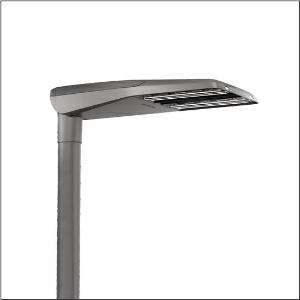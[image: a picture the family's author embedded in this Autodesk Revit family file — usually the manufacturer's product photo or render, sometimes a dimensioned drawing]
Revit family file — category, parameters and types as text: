
# Revit family: streetlight_sl_11_iq_midi___st1_0a_5xc3m41f08le_9450
name_source: partatom
category: Lighting Fixtures
units: mm (PartAtom-declared; Revit-internal decimal feet)

## family parameters
Cut with Voids When Loaded = No
Host = Face
Light Source = No
Part Type = Normal
Room Calculation Point = No
Round Connector Dimension = Use Diameter
Shared = No

## types (1)
- --- (1 x LED, 9290 lm, 60.4 W, 4000K)
    Apparent Load = 60 VA
    CIE Flux Codes = 33 66 96 100 100
    Color Rendering = 70
    Color Temperature = 4000K
    Default Elevation = 1800 mm
    Description = Streetlight SL 11 iQ midi, mast luminaire, primary light control with 3 zone facetted reflector, of plastic, silver coated, highly specular, primary optical cover: cover, of PMMA, transparent, light distribution: ST1.0a, light emission: direct distribution, primary light characteristic: asymmetric, installation type: post-top, side-entry, LED, High Power LED, rated luminous flux: 9.290lm, luminous efficacy: 154lm/W, light colour: 740, colour temperature: 4000K, control: optimised constant luminous flux control (CLO 2.0), Street-Remote, Desk-Remote (wireless, voltage-free reading and setting of iQ features in the workshop via application-optimized NFC function/RFID function), Light-Fading, Smart-Wire, Night-Set, Lumen-Switch, Temp-Guard, Auto-Match, with cable H07RN-F 5x 1.5mm², mains connection: 230..240V, AC, 50/60Hz, connection cable pre-assembled, cable length: 8,5m, start of lifetime: 60W, end of service life: 63W, reduction: 30W, luminaire housing, of diecast aluminium, powder-coated, Siteco® metallic grey (DB 702S), please order mast flange separately, inclination adjustable without tools: 0°, 5°, 10°, 15° (post-top) | 0°, -5°, -10°, -15° (side-entry), sealing non-destructively replaceable, multi-level sealing system, length: 780mm, width: 376mm, height: 118mm, mast flange for spigot size: 42mm (side-entry): 5XC10008XM4, 60/48mm (side-entry/post-top): 5XC10108XM2, 76/60mm (side-entry/post-top): 5XC10108XM1, equipment: standard, protection rating (complete): IP66, insulation class (complete): insulation class II (safety insulation), certification: CE, ENEC, VDE, impact resistance: IK09, permissible operating ambient temperature for outdoor applications: -25..+50°C, standard-compliant lighting for roads and squares, Environmental Product Declaration (EPD) tested and certified by an independent institute, packaging unit: 1 piece

Light Distribution: ST1.0a
    Height = 118 mm
    Lamp = 1 x LED
    Lamp Light Flux = 9290 lm
    Lamp Power = 60.4 W
    Lamp count = 1
    Length = 780 mm
    Luminous efficacy = 154 lm/W
    Manufacturer = Siteco
    ModVariant = No
    Model = 5XC3M41F08LE
    Number of Poles = 1
    OnlyDefault = Yes
    Power Factor = 1
    Product Name = Streetlight SL 11 iQ midi | ST1.0a
    Product group = mast luminaire | pylon top
    ProductGroupID = 6100
    Protection Class = Protection class II
    Protection Degree = IP 66
    RLX_Detail_Level = 1
    RLX_Emergency_Light_Flux = 0 lm
    RLX_Emergency_Type = 0
    RLX_Emergency_Type_DB = No
    RlxData = <blob elided: 70201 chars, md5=ece78375>
    Socket = socket
    Standby Power = 0 W
    System Light Flux = 9290 lm
    System Power = 60 W
    Type Comments = factory setting: luminous flux: 100 % | dim-lin: 254 | 520 mA
    Type Image = l_1005960.jpg
    URL = http://relux.com
    VarID = @adj_020891
    Voltage = 0 V
    Weight = 0.00 kg
    Width = 376 mm

## geometry (parser evidence)
native form markers: Blend x4, Sweep x10
no freeform markers — native parametric forms only
